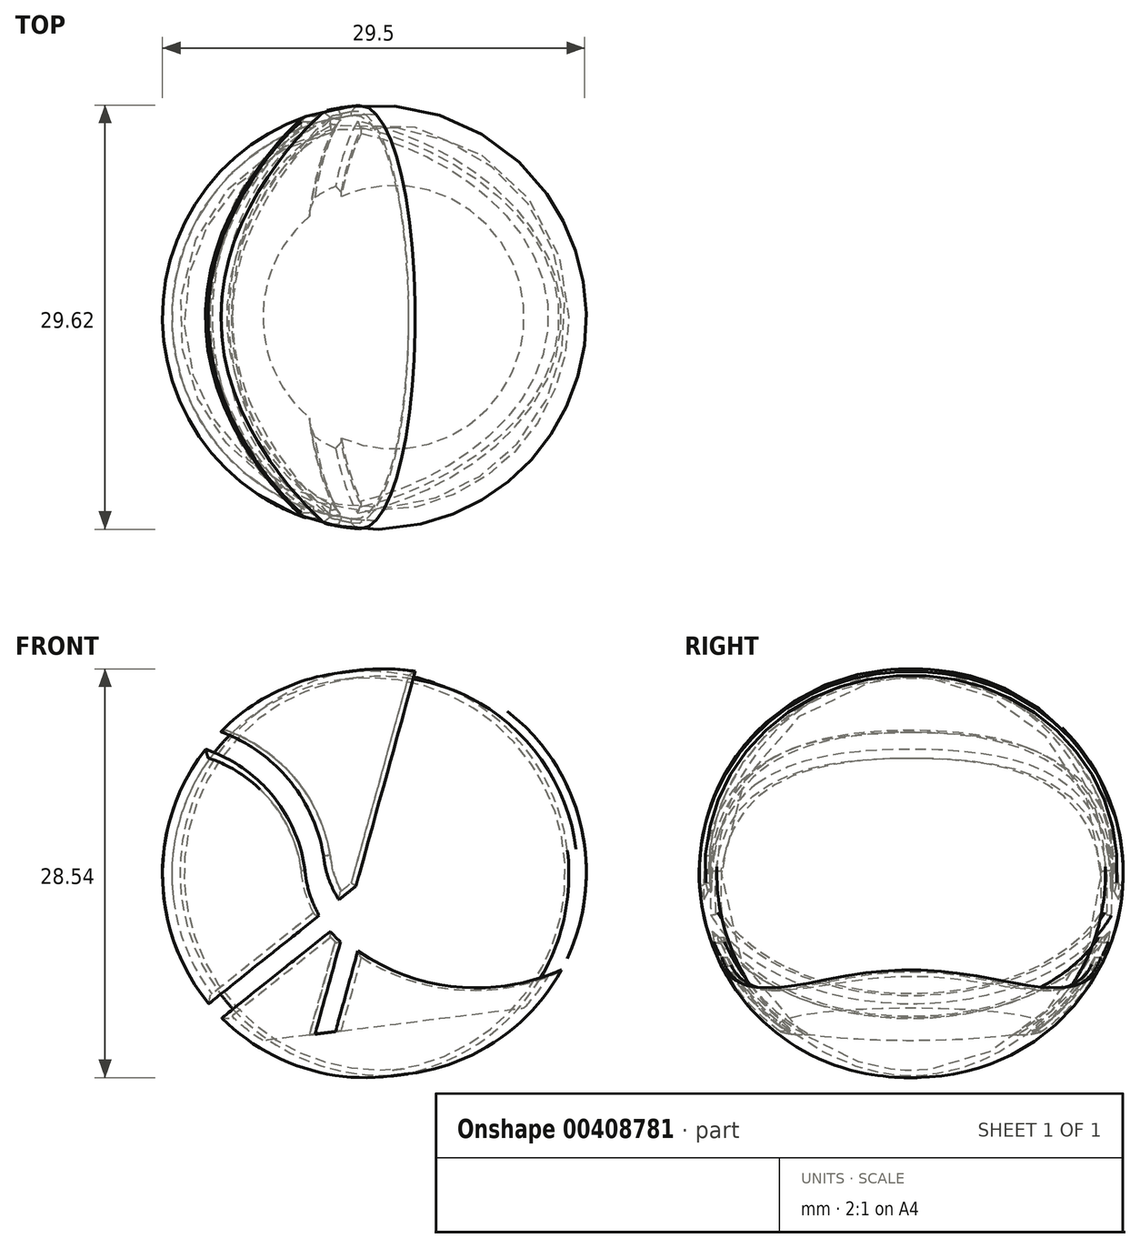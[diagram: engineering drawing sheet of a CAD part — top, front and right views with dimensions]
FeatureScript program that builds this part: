
annotation { "Feature Type Name" : "Feature", "Feature Type Description" : "" }
export const myFeature = defineFeature(function(context is Context, id is Id, definition is map)
    precondition{}
    {
        {
            var Q0;
            Q0=qCreatedBy(makeId("Front.planeOp"),FACE);
            var sketch = newSketch(context, id + "F0", { "sketchPlane" : qUnion([Q0])});
            skLineSegment(sketch, "E0", {"start": v(-42.37, 14.43) * mm, "end": v(-51.36, 13.33) * mm});
            skLineSegment(sketch, "E1", {"start": v(-51.36, 13.33) * mm, "end": v(-54.34, 37.59) * mm});
            skArc(sketch, "E2", {"start": v(-42.37, 14.43) * mm, "mid": v(-40.03, 30.31) * mm, "end": v(-54.34, 37.59) * mm});
            skSolve(sketch);
        }
        {
            var Q0;
            Q0=makeQuery(id+"F0.imprint","IMPRINT",FACE,{"disambiguationData":[TD([[makeQuery(id+"F0.imprint","IMPRINT",EDGE,{"derivedFrom":sQuery(id+"F0.wireOp",EDGE,"E0")}),-1.0]])]});
            var Q1;
            Q1=sQuery(id+"F0.wireOp",EDGE,"E1");
            revolve(context, id + "F1", {"entities" : qUnion([Q0]), "axis" : qUnion([Q1]), "revolveType" : RevolveType.FULL});
        }
        {
            var Q0;
            Q0=qCreatedBy(makeId("Front.planeOp"),FACE);
            var sketch = newSketch(context, id + "F2", { "sketchPlane" : qUnion([Q0])});
            skLineSegment(sketch, "E3", {"start": v(-47.67, 39.48) * mm, "end": v(-56.18, 8.75) * mm});
            skLineSegment(sketch, "E4", {"start": v(-56.18, 8.75) * mm, "end": v(-58.16, 9.3) * mm});
            skLineSegment(sketch, "E5", {"start": v(-58.16, 9.3) * mm, "end": v(-49.8, 39.48) * mm});
            skLineSegment(sketch, "E6", {"start": v(-49.8, 39.48) * mm, "end": v(-47.67, 39.48) * mm});
            skLineSegment(sketch, "E7", {"start": v(-65.5, 11.74) * mm, "end": v(-37.78, 33.85) * mm});
            skLineSegment(sketch, "E8", {"start": v(-37.78, 33.85) * mm, "end": v(-39.07, 35.47) * mm});
            skLineSegment(sketch, "E9", {"start": v(-39.07, 35.47) * mm, "end": v(-66.87, 13.3) * mm});
            skLineSegment(sketch, "E10", {"start": v(-66.87, 13.3) * mm, "end": v(-65.5, 11.74) * mm});
            skArc(sketch, "E11", {"start": v(-52.97, 20.32) * mm, "mid": v(-44.78, 17.68) * mm, "end": v(-37.04, 21.45) * mm});
            skPoint(sketch, "E11.startSnap0", {"position": v(-52.97, 24.38) * mm});
            skArc(sketch, "E12", {"start": v(-55.76, 25.21) * mm, "mid": v(-55.5, 23.95) * mm, "end": v(-55, 22.77) * mm});
            skArc(sketch, "E13", {"start": v(-55.76, 25.21) * mm, "mid": v(-58.82, 31.27) * mm, "end": v(-64.8, 34.46) * mm});
            skArc(sketch, "E14", {"start": v(-53.58, 18.12) * mm, "mid": v(-44.85, 15.85) * mm, "end": v(-36.46, 19.17) * mm});
            skArc(sketch, "E15", {"start": v(-57.79, 24.15) * mm, "mid": v(-57.05, 21.47) * mm, "end": v(-55.42, 19.21) * mm});
            skArc(sketch, "E16", {"start": v(-57.79, 24.15) * mm, "mid": v(-60.6, 29.8) * mm, "end": v(-66.32, 32.5) * mm});
            skLineSegment(sketch, "E17", {"start": v(-64.8, 34.46) * mm, "end": v(-66.32, 32.5) * mm});
            skLineSegment(sketch, "E18", {"start": v(-37.04, 21.45) * mm, "end": v(-36.46, 19.17) * mm});
            skSolve(sketch);
        }
        {
            var Q0;
            Q0 = qSketchRegion(id + "F2", true);
            extrude(context, id + "F3", {"entities" : qUnion([Q0]), "operationType" : NewBodyOperationType.ADD, "depth" : 18.8 * mm, "offsetDistance" : 25.4 * mm, "hasSecondDirection" : true, "secondDirectionOppositeDirection" : true, "secondDirectionDepth" : 18.8 * mm});
        }
        {
            var Q0;
            Q0=qCreatedBy(makeId("Front.planeOp"),FACE);
            var sketch = newSketch(context, id + "F4", { "sketchPlane" : qUnion([Q0])});
            skLineSegment(sketch, "E19", {"start": v(-54.57, 38.95) * mm, "end": v(-50.05, 3.12) * mm});
            skArc(sketch, "E20", {"start": v(-41.9, 14.18) * mm, "mid": v(-39.5, 30.68) * mm, "end": v(-54.46, 38.07) * mm});
            skLineSegment(sketch, "E21", {"start": v(-51.35, 13.45) * mm, "end": v(-41.4, 14.7) * mm});
            skLineSegment(sketch, "E22", {"start": v(-54.57, 38.95) * mm, "end": v(-55, 42.45) * mm});
            skLineSegment(sketch, "E23", {"start": v(-55, 42.45) * mm, "end": v(-20.73, 44.43) * mm});
            skLineSegment(sketch, "E24", {"start": v(-16.5, 6.68) * mm, "end": v(-50.05, 3.12) * mm});
            skLineSegment(sketch, "E25", {"start": v(-20.73, 44.43) * mm, "end": v(-16.5, 6.68) * mm});
            skSolve(sketch);
        }
        {
            var Q0;
            {var subQ0=sQuery(id+"F4.wireOp",EDGE,"E21");Q0=makeQuery(id+"F4.imprint","IMPRINT",FACE,{"disambiguationData":[TD([[makeQuery(id+"F4.imprint","IMPRINT",EDGE,{"derivedFrom":subQ0}),-1.0]])]});}
            var Q1;
            Q1=sQuery(id+"F4.wireOp",EDGE,"E19");
            revolve(context, id + "F5", {"operationType" : NewBodyOperationType.REMOVE, "entities" : qUnion([Q0]), "axis" : qUnion([Q1]), "revolveType" : RevolveType.FULL, "oppositeDirection" : true});
        }
        {
            var Q0;
            {var subQ0=sQuery(id+"F2.wireOp",EDGE,"E11");var subQ1=sQuery(id+"F2.wireOp",EDGE,"E8");var subQ2=sQuery(id+"F2.wireOp",EDGE,"E7");var subQ3=sQuery(id+"F2.wireOp",EDGE,"E3");Q0=makeQuery(id+"F5.boolean.opBoolean","INTERSECT",EDGE,{"derivedFrom":[makeQuery(id+"F3.boolean.opBoolean","SPLIT",FACE,{"disambiguationData":[TD([makeQuery(id+"F3.opExtrude","CAP_FACE",FACE,{"disambiguationData":[OSD([subQ3,sQuery(id+"F2.wireOp",EDGE,"E4"),sQuery(id+"F2.wireOp",EDGE,"E5"),sQuery(id+"F2.wireOp",EDGE,"E6"),subQ2,subQ1,sQuery(id+"F2.wireOp",EDGE,"E9"),sQuery(id+"F2.wireOp",EDGE,"E10"),subQ0,sQuery(id+"F2.wireOp",EDGE,"E12"),sQuery(id+"F2.wireOp",EDGE,"E13"),sQuery(id+"F2.wireOp",EDGE,"E14"),sQuery(id+"F2.wireOp",EDGE,"E15"),sQuery(id+"F2.wireOp",EDGE,"E16"),sQuery(id+"F2.wireOp",EDGE,"E17"),sQuery(id+"F2.wireOp",EDGE,"E18")])],"isStart":true})])],"derivedFrom":makeQuery(id+"F3.opExtrude","SWEPT_FACE",FACE,{"disambiguationData":[OSD([subQ3]),TDD([makeQuery(id+"F2.imprint","IMPRINT",EDGE,{"disambiguationData":[TD([[makeQuery(id+"F2.imprint","INTERSECT",VERTEX,{"derivedFrom":[subQ3,subQ0]}),1.0]])],"derivedFrom":subQ3})])]})}),makeQuery(id+"F5.opRevolve","SWEPT_FACE",FACE,{"disambiguationData":[OSD([sQuery(id+"F4.wireOp",EDGE,"E20")])]})]});}
            var Q1;
            Q1=makeQuery(id+"F5.boolean.opBoolean","INTERSECT",EDGE,{"derivedFrom":[makeQuery(id+"F3.opExtrude","SWEPT_FACE",FACE,{"disambiguationData":[OSD([sQuery(id+"F2.wireOp",EDGE,"E11")])]}),makeQuery(id+"F5.opRevolve","SWEPT_FACE",FACE,{"disambiguationData":[OSD([sQuery(id+"F4.wireOp",EDGE,"E20")])]})]});
            var Q2;
            {var subQ0=sQuery(id+"F2.wireOp",EDGE,"E7");Q2=makeQuery(id+"F5.boolean.opBoolean","INTERSECT",EDGE,{"derivedFrom":[makeQuery(id+"F3.opExtrude","SWEPT_FACE",FACE,{"disambiguationData":[OSD([subQ0]),TDD([makeQuery(id+"F2.imprint","IMPRINT",EDGE,{"disambiguationData":[TD([[makeQuery(id+"F2.imprint","INTERSECT",VERTEX,{"derivedFrom":[subQ0,sQuery(id+"F2.wireOp",EDGE,"E8")]}),1.0]])],"derivedFrom":subQ0})])]}),makeQuery(id+"F5.opRevolve","SWEPT_FACE",FACE,{"disambiguationData":[OSD([sQuery(id+"F4.wireOp",EDGE,"E20")])]})]});}
            var Q3;
            Q3=makeQuery(id+"F5.boolean.opBoolean","INTERSECT",EDGE,{"derivedFrom":[makeQuery(id+"F3.opExtrude","SWEPT_FACE",FACE,{"disambiguationData":[OSD([sQuery(id+"F2.wireOp",EDGE,"E14")])]}),makeQuery(id+"F5.opRevolve","SWEPT_FACE",FACE,{"disambiguationData":[OSD([sQuery(id+"F4.wireOp",EDGE,"E20")])]})]});
            var Q4;
            {var subQ0=sQuery(id+"F2.wireOp",EDGE,"E3");Q4=makeQuery(id+"F5.boolean.opBoolean","INTERSECT",EDGE,{"disambiguationData":[OD(0.0)],"derivedFrom":[makeQuery(id+"F3.opExtrude","SWEPT_FACE",FACE,{"disambiguationData":[OSD([subQ0]),TDD([makeQuery(id+"F2.imprint","IMPRINT",EDGE,{"disambiguationData":[TD([[makeQuery(id+"F2.imprint","INTERSECT",VERTEX,{"derivedFrom":[subQ0,sQuery(id+"F2.wireOp",EDGE,"E4")]}),1.0]])],"derivedFrom":subQ0})])]}),makeQuery(id+"F5.opRevolve","SWEPT_FACE",FACE,{"disambiguationData":[OSD([sQuery(id+"F4.wireOp",EDGE,"E20")])]})]});}
            var Q5;
            {var subQ0=sQuery(id+"F2.wireOp",EDGE,"E15");var subQ1=sQuery(id+"F2.wireOp",EDGE,"E10");var subQ2=sQuery(id+"F2.wireOp",EDGE,"E7");var subQ3=sQuery(id+"F2.wireOp",EDGE,"E5");var subQ4=sQuery(id+"F2.wireOp",EDGE,"E4");var subQ5=makeQuery(id+"F2.imprint","INTERSECT",VERTEX,{"derivedFrom":[subQ3,subQ0]});Q5=makeQuery(id+"F5.boolean.opBoolean","INTERSECT",EDGE,{"derivedFrom":[makeQuery(id+"F3.boolean.opBoolean","SPLIT",FACE,{"disambiguationData":[TD([makeQuery(id+"F3.opExtrude","CAP_FACE",FACE,{"disambiguationData":[OSD([sQuery(id+"F2.wireOp",EDGE,"E3"),subQ4,subQ3,sQuery(id+"F2.wireOp",EDGE,"E6"),subQ2,sQuery(id+"F2.wireOp",EDGE,"E8"),sQuery(id+"F2.wireOp",EDGE,"E9"),subQ1,sQuery(id+"F2.wireOp",EDGE,"E11"),sQuery(id+"F2.wireOp",EDGE,"E12"),sQuery(id+"F2.wireOp",EDGE,"E13"),sQuery(id+"F2.wireOp",EDGE,"E14"),subQ0,sQuery(id+"F2.wireOp",EDGE,"E16"),sQuery(id+"F2.wireOp",EDGE,"E17"),sQuery(id+"F2.wireOp",EDGE,"E18")])],"isStart":true})])],"derivedFrom":makeQuery(id+"F3.opExtrude","SWEPT_FACE",FACE,{"disambiguationData":[OSD([subQ0]),TDD([makeQuery(id+"F2.imprint","IMPRINT",EDGE,{"disambiguationData":[TD([[subQ5,1.0]])],"derivedFrom":subQ0})])]})}),makeQuery(id+"F5.opRevolve","SWEPT_FACE",FACE,{"disambiguationData":[OSD([sQuery(id+"F4.wireOp",EDGE,"E20")])]})]});}
            var Q6;
            {var subQ0=sQuery(id+"F2.wireOp",EDGE,"E5");Q6=makeQuery(id+"F5.boolean.opBoolean","INTERSECT",EDGE,{"disambiguationData":[OD(0.0)],"derivedFrom":[makeQuery(id+"F3.opExtrude","SWEPT_FACE",FACE,{"disambiguationData":[OSD([subQ0]),TDD([makeQuery(id+"F2.imprint","IMPRINT",EDGE,{"disambiguationData":[TD([[makeQuery(id+"F2.imprint","INTERSECT",VERTEX,{"derivedFrom":[sQuery(id+"F2.wireOp",EDGE,"E4"),subQ0]}),-1.0]])],"derivedFrom":subQ0})])]}),makeQuery(id+"F5.opRevolve","SWEPT_FACE",FACE,{"disambiguationData":[OSD([sQuery(id+"F4.wireOp",EDGE,"E20")])]})]});}
            var Q7;
            {var subQ0=sQuery(id+"F2.wireOp",EDGE,"E7");Q7=makeQuery(id+"F5.boolean.opBoolean","INTERSECT",EDGE,{"derivedFrom":[makeQuery(id+"F3.opExtrude","SWEPT_FACE",FACE,{"disambiguationData":[OSD([subQ0]),TDD([makeQuery(id+"F2.imprint","IMPRINT",EDGE,{"disambiguationData":[TD([[makeQuery(id+"F2.imprint","INTERSECT",VERTEX,{"derivedFrom":[subQ0,sQuery(id+"F2.wireOp",EDGE,"E10")]}),-1.0]])],"derivedFrom":subQ0})])]}),makeQuery(id+"F5.opRevolve","SWEPT_FACE",FACE,{"disambiguationData":[OSD([sQuery(id+"F4.wireOp",EDGE,"E20")])]})]});}
            var Q8;
            {var subQ0=sQuery(id+"F2.wireOp",EDGE,"E9");Q8=makeQuery(id+"F5.boolean.opBoolean","INTERSECT",EDGE,{"derivedFrom":[makeQuery(id+"F3.opExtrude","SWEPT_FACE",FACE,{"disambiguationData":[OSD([subQ0]),TDD([makeQuery(id+"F2.imprint","IMPRINT",EDGE,{"disambiguationData":[TD([[makeQuery(id+"F2.imprint","INTERSECT",VERTEX,{"derivedFrom":[sQuery(id+"F2.wireOp",EDGE,"E8"),subQ0]}),-1.0]])],"derivedFrom":subQ0})])]}),makeQuery(id+"F5.opRevolve","SWEPT_FACE",FACE,{"disambiguationData":[OSD([sQuery(id+"F4.wireOp",EDGE,"E20")])]})]});}
            var Q9;
            {var subQ0=sQuery(id+"F2.wireOp",EDGE,"E3");Q9=makeQuery(id+"F5.boolean.opBoolean","INTERSECT",EDGE,{"derivedFrom":[makeQuery(id+"F3.opExtrude","SWEPT_FACE",FACE,{"disambiguationData":[OSD([subQ0]),TDD([makeQuery(id+"F2.imprint","IMPRINT",EDGE,{"disambiguationData":[TD([[makeQuery(id+"F2.imprint","INTERSECT",VERTEX,{"derivedFrom":[subQ0,sQuery(id+"F2.wireOp",EDGE,"E6")]}),-1.0]])],"derivedFrom":subQ0})])]}),makeQuery(id+"F5.opRevolve","SWEPT_FACE",FACE,{"disambiguationData":[OSD([sQuery(id+"F4.wireOp",EDGE,"E20")])]})]});}
            var Q10;
            {var subQ0=sQuery(id+"F2.wireOp",EDGE,"E5");Q10=makeQuery(id+"F5.boolean.opBoolean","INTERSECT",EDGE,{"derivedFrom":[makeQuery(id+"F3.opExtrude","SWEPT_FACE",FACE,{"disambiguationData":[OSD([subQ0]),TDD([makeQuery(id+"F2.imprint","IMPRINT",EDGE,{"disambiguationData":[TD([[makeQuery(id+"F2.imprint","INTERSECT",VERTEX,{"derivedFrom":[subQ0,sQuery(id+"F2.wireOp",EDGE,"E6")]}),1.0]])],"derivedFrom":subQ0})])]}),makeQuery(id+"F5.opRevolve","SWEPT_FACE",FACE,{"disambiguationData":[OSD([sQuery(id+"F4.wireOp",EDGE,"E20")])]})]});}
            var Q11;
            {var subQ0=sQuery(id+"F2.wireOp",EDGE,"E12");var subQ1=sQuery(id+"F2.wireOp",EDGE,"E9");var subQ2=sQuery(id+"F2.wireOp",EDGE,"E6");var subQ3=sQuery(id+"F2.wireOp",EDGE,"E5");Q11=makeQuery(id+"F5.boolean.opBoolean","INTERSECT",EDGE,{"derivedFrom":[makeQuery(id+"F3.boolean.opBoolean","SPLIT",FACE,{"disambiguationData":[TD([makeQuery(id+"F3.opExtrude","CAP_FACE",FACE,{"disambiguationData":[OSD([sQuery(id+"F2.wireOp",EDGE,"E3"),sQuery(id+"F2.wireOp",EDGE,"E4"),subQ3,subQ2,sQuery(id+"F2.wireOp",EDGE,"E7"),sQuery(id+"F2.wireOp",EDGE,"E8"),subQ1,sQuery(id+"F2.wireOp",EDGE,"E10"),sQuery(id+"F2.wireOp",EDGE,"E11"),subQ0,sQuery(id+"F2.wireOp",EDGE,"E13"),sQuery(id+"F2.wireOp",EDGE,"E14"),sQuery(id+"F2.wireOp",EDGE,"E15"),sQuery(id+"F2.wireOp",EDGE,"E16"),sQuery(id+"F2.wireOp",EDGE,"E17"),sQuery(id+"F2.wireOp",EDGE,"E18")])],"isStart":true})])],"derivedFrom":makeQuery(id+"F3.opExtrude","SWEPT_FACE",FACE,{"disambiguationData":[OSD([subQ1]),TDD([makeQuery(id+"F2.imprint","IMPRINT",EDGE,{"disambiguationData":[TD([[makeQuery(id+"F2.imprint","INTERSECT",VERTEX,{"derivedFrom":[subQ1,subQ0]}),1.0]])],"derivedFrom":subQ1})])]})}),makeQuery(id+"F5.opRevolve","SWEPT_FACE",FACE,{"disambiguationData":[OSD([sQuery(id+"F4.wireOp",EDGE,"E20")])]})]});}
            var Q12;
            {var subQ0=sQuery(id+"F2.wireOp",EDGE,"E12");var subQ1=sQuery(id+"F2.wireOp",EDGE,"E9");var subQ2=sQuery(id+"F2.wireOp",EDGE,"E5");var subQ3=sQuery(id+"F2.wireOp",EDGE,"E13");Q12=makeQuery(id+"F5.boolean.opBoolean","INTERSECT",EDGE,{"derivedFrom":[makeQuery(id+"F3.boolean.opBoolean","SPLIT",FACE,{"disambiguationData":[TD([makeQuery(id+"F3.opExtrude","CAP_FACE",FACE,{"disambiguationData":[OSD([sQuery(id+"F2.wireOp",EDGE,"E3"),sQuery(id+"F2.wireOp",EDGE,"E4"),subQ2,sQuery(id+"F2.wireOp",EDGE,"E6"),sQuery(id+"F2.wireOp",EDGE,"E7"),sQuery(id+"F2.wireOp",EDGE,"E8"),subQ1,sQuery(id+"F2.wireOp",EDGE,"E10"),sQuery(id+"F2.wireOp",EDGE,"E11"),subQ0,subQ3,sQuery(id+"F2.wireOp",EDGE,"E14"),sQuery(id+"F2.wireOp",EDGE,"E15"),sQuery(id+"F2.wireOp",EDGE,"E16"),sQuery(id+"F2.wireOp",EDGE,"E17"),sQuery(id+"F2.wireOp",EDGE,"E18")])],"isStart":true})])],"derivedFrom":makeQuery(id+"F3.opExtrude","SWEPT_FACE",FACE,{"disambiguationData":[OSD([subQ0])]})}),makeQuery(id+"F5.opRevolve","SWEPT_FACE",FACE,{"disambiguationData":[OSD([sQuery(id+"F4.wireOp",EDGE,"E20")])]})]});}
            var Q13;
            Q13=makeQuery(id+"F5.boolean.opBoolean","INTERSECT",EDGE,{"derivedFrom":[makeQuery(id+"F3.opExtrude","SWEPT_FACE",FACE,{"disambiguationData":[OSD([sQuery(id+"F2.wireOp",EDGE,"E13")])]}),makeQuery(id+"F5.opRevolve","SWEPT_FACE",FACE,{"disambiguationData":[OSD([sQuery(id+"F4.wireOp",EDGE,"E20")])]})]});
            var Q14;
            Q14=makeQuery(id+"F5.boolean.opBoolean","INTERSECT",EDGE,{"derivedFrom":[makeQuery(id+"F3.opExtrude","SWEPT_FACE",FACE,{"disambiguationData":[OSD([sQuery(id+"F2.wireOp",EDGE,"E16")])]}),makeQuery(id+"F5.opRevolve","SWEPT_FACE",FACE,{"disambiguationData":[OSD([sQuery(id+"F4.wireOp",EDGE,"E20")])]})]});
            var Q15;
            {var subQ0=sQuery(id+"F2.wireOp",EDGE,"E16");var subQ1=sQuery(id+"F2.wireOp",EDGE,"E15");var subQ2=sQuery(id+"F2.wireOp",EDGE,"E10");var subQ3=sQuery(id+"F2.wireOp",EDGE,"E9");Q15=makeQuery(id+"F5.boolean.opBoolean","INTERSECT",EDGE,{"derivedFrom":[makeQuery(id+"F3.boolean.opBoolean","SPLIT",FACE,{"disambiguationData":[TD([makeQuery(id+"F3.opExtrude","CAP_FACE",FACE,{"disambiguationData":[OSD([sQuery(id+"F2.wireOp",EDGE,"E3"),sQuery(id+"F2.wireOp",EDGE,"E4"),sQuery(id+"F2.wireOp",EDGE,"E5"),sQuery(id+"F2.wireOp",EDGE,"E6"),sQuery(id+"F2.wireOp",EDGE,"E7"),sQuery(id+"F2.wireOp",EDGE,"E8"),subQ3,subQ2,sQuery(id+"F2.wireOp",EDGE,"E11"),sQuery(id+"F2.wireOp",EDGE,"E12"),sQuery(id+"F2.wireOp",EDGE,"E13"),sQuery(id+"F2.wireOp",EDGE,"E14"),subQ1,subQ0,sQuery(id+"F2.wireOp",EDGE,"E17"),sQuery(id+"F2.wireOp",EDGE,"E18")])],"isStart":true})])],"derivedFrom":makeQuery(id+"F3.opExtrude","SWEPT_FACE",FACE,{"disambiguationData":[OSD([subQ1]),TDD([makeQuery(id+"F2.imprint","IMPRINT",EDGE,{"disambiguationData":[TD([[makeQuery(id+"F2.imprint","INTERSECT",VERTEX,{"derivedFrom":[subQ1,subQ0]}),-1.0]])],"derivedFrom":subQ1})])]})}),makeQuery(id+"F5.opRevolve","SWEPT_FACE",FACE,{"disambiguationData":[OSD([sQuery(id+"F4.wireOp",EDGE,"E20")])]})]});}
            var Q16;
            {var subQ0=sQuery(id+"F2.wireOp",EDGE,"E9");Q16=makeQuery(id+"F5.boolean.opBoolean","INTERSECT",EDGE,{"derivedFrom":[makeQuery(id+"F3.opExtrude","SWEPT_FACE",FACE,{"disambiguationData":[OSD([subQ0]),TDD([makeQuery(id+"F2.imprint","IMPRINT",EDGE,{"disambiguationData":[TD([[makeQuery(id+"F2.imprint","INTERSECT",VERTEX,{"derivedFrom":[subQ0,sQuery(id+"F2.wireOp",EDGE,"E10")]}),1.0]])],"derivedFrom":subQ0})])]}),makeQuery(id+"F5.opRevolve","SWEPT_FACE",FACE,{"disambiguationData":[OSD([sQuery(id+"F4.wireOp",EDGE,"E20")])]})]});}
            var Q17;
            {var subQ0=sQuery(id+"F2.wireOp",EDGE,"E16");var subQ1=sQuery(id+"F2.wireOp",EDGE,"E15");var subQ2=sQuery(id+"F2.wireOp",EDGE,"E10");var subQ3=sQuery(id+"F2.wireOp",EDGE,"E9");Q17=makeQuery(id+"F5.boolean.opBoolean","INTERSECT",EDGE,{"derivedFrom":[makeQuery(id+"F3.boolean.opBoolean","SPLIT",FACE,{"disambiguationData":[TD([makeQuery(id+"F3.opExtrude","CAP_FACE",FACE,{"disambiguationData":[OSD([sQuery(id+"F2.wireOp",EDGE,"E3"),sQuery(id+"F2.wireOp",EDGE,"E4"),sQuery(id+"F2.wireOp",EDGE,"E5"),sQuery(id+"F2.wireOp",EDGE,"E6"),sQuery(id+"F2.wireOp",EDGE,"E7"),sQuery(id+"F2.wireOp",EDGE,"E8"),subQ3,subQ2,sQuery(id+"F2.wireOp",EDGE,"E11"),sQuery(id+"F2.wireOp",EDGE,"E12"),sQuery(id+"F2.wireOp",EDGE,"E13"),sQuery(id+"F2.wireOp",EDGE,"E14"),subQ1,subQ0,sQuery(id+"F2.wireOp",EDGE,"E17"),sQuery(id+"F2.wireOp",EDGE,"E18")])],"isStart":false})])],"derivedFrom":makeQuery(id+"F3.opExtrude","SWEPT_FACE",FACE,{"disambiguationData":[OSD([subQ1]),TDD([makeQuery(id+"F2.imprint","IMPRINT",EDGE,{"disambiguationData":[TD([[makeQuery(id+"F2.imprint","INTERSECT",VERTEX,{"derivedFrom":[subQ1,subQ0]}),-1.0]])],"derivedFrom":subQ1})])]})}),makeQuery(id+"F5.opRevolve","SWEPT_FACE",FACE,{"disambiguationData":[OSD([sQuery(id+"F4.wireOp",EDGE,"E20")])]})]});}
            var Q18;
            {var subQ0=sQuery(id+"F2.wireOp",EDGE,"E12");var subQ1=sQuery(id+"F2.wireOp",EDGE,"E9");var subQ2=sQuery(id+"F2.wireOp",EDGE,"E5");var subQ3=sQuery(id+"F2.wireOp",EDGE,"E13");Q18=makeQuery(id+"F5.boolean.opBoolean","INTERSECT",EDGE,{"derivedFrom":[makeQuery(id+"F3.boolean.opBoolean","SPLIT",FACE,{"disambiguationData":[TD([makeQuery(id+"F3.opExtrude","CAP_FACE",FACE,{"disambiguationData":[OSD([sQuery(id+"F2.wireOp",EDGE,"E3"),sQuery(id+"F2.wireOp",EDGE,"E4"),subQ2,sQuery(id+"F2.wireOp",EDGE,"E6"),sQuery(id+"F2.wireOp",EDGE,"E7"),sQuery(id+"F2.wireOp",EDGE,"E8"),subQ1,sQuery(id+"F2.wireOp",EDGE,"E10"),sQuery(id+"F2.wireOp",EDGE,"E11"),subQ0,subQ3,sQuery(id+"F2.wireOp",EDGE,"E14"),sQuery(id+"F2.wireOp",EDGE,"E15"),sQuery(id+"F2.wireOp",EDGE,"E16"),sQuery(id+"F2.wireOp",EDGE,"E17"),sQuery(id+"F2.wireOp",EDGE,"E18")])],"isStart":false})])],"derivedFrom":makeQuery(id+"F3.opExtrude","SWEPT_FACE",FACE,{"disambiguationData":[OSD([subQ0])]})}),makeQuery(id+"F5.opRevolve","SWEPT_FACE",FACE,{"disambiguationData":[OSD([sQuery(id+"F4.wireOp",EDGE,"E20")])]})]});}
            var Q19;
            {var subQ0=sQuery(id+"F2.wireOp",EDGE,"E12");var subQ1=sQuery(id+"F2.wireOp",EDGE,"E9");var subQ2=sQuery(id+"F2.wireOp",EDGE,"E6");var subQ3=sQuery(id+"F2.wireOp",EDGE,"E5");Q19=makeQuery(id+"F5.boolean.opBoolean","INTERSECT",EDGE,{"derivedFrom":[makeQuery(id+"F3.boolean.opBoolean","SPLIT",FACE,{"disambiguationData":[TD([makeQuery(id+"F3.opExtrude","CAP_FACE",FACE,{"disambiguationData":[OSD([sQuery(id+"F2.wireOp",EDGE,"E3"),sQuery(id+"F2.wireOp",EDGE,"E4"),subQ3,subQ2,sQuery(id+"F2.wireOp",EDGE,"E7"),sQuery(id+"F2.wireOp",EDGE,"E8"),subQ1,sQuery(id+"F2.wireOp",EDGE,"E10"),sQuery(id+"F2.wireOp",EDGE,"E11"),subQ0,sQuery(id+"F2.wireOp",EDGE,"E13"),sQuery(id+"F2.wireOp",EDGE,"E14"),sQuery(id+"F2.wireOp",EDGE,"E15"),sQuery(id+"F2.wireOp",EDGE,"E16"),sQuery(id+"F2.wireOp",EDGE,"E17"),sQuery(id+"F2.wireOp",EDGE,"E18")])],"isStart":false})])],"derivedFrom":makeQuery(id+"F3.opExtrude","SWEPT_FACE",FACE,{"disambiguationData":[OSD([subQ1]),TDD([makeQuery(id+"F2.imprint","IMPRINT",EDGE,{"disambiguationData":[TD([[makeQuery(id+"F2.imprint","INTERSECT",VERTEX,{"derivedFrom":[subQ1,subQ0]}),1.0]])],"derivedFrom":subQ1})])]})}),makeQuery(id+"F5.opRevolve","SWEPT_FACE",FACE,{"disambiguationData":[OSD([sQuery(id+"F4.wireOp",EDGE,"E20")])]})]});}
            var Q20;
            {var subQ0=sQuery(id+"F2.wireOp",EDGE,"E11");var subQ1=sQuery(id+"F2.wireOp",EDGE,"E8");var subQ2=sQuery(id+"F2.wireOp",EDGE,"E7");var subQ3=sQuery(id+"F2.wireOp",EDGE,"E3");Q20=makeQuery(id+"F5.boolean.opBoolean","INTERSECT",EDGE,{"derivedFrom":[makeQuery(id+"F3.boolean.opBoolean","SPLIT",FACE,{"disambiguationData":[TD([makeQuery(id+"F3.opExtrude","CAP_FACE",FACE,{"disambiguationData":[OSD([subQ3,sQuery(id+"F2.wireOp",EDGE,"E4"),sQuery(id+"F2.wireOp",EDGE,"E5"),sQuery(id+"F2.wireOp",EDGE,"E6"),subQ2,subQ1,sQuery(id+"F2.wireOp",EDGE,"E9"),sQuery(id+"F2.wireOp",EDGE,"E10"),subQ0,sQuery(id+"F2.wireOp",EDGE,"E12"),sQuery(id+"F2.wireOp",EDGE,"E13"),sQuery(id+"F2.wireOp",EDGE,"E14"),sQuery(id+"F2.wireOp",EDGE,"E15"),sQuery(id+"F2.wireOp",EDGE,"E16"),sQuery(id+"F2.wireOp",EDGE,"E17"),sQuery(id+"F2.wireOp",EDGE,"E18")])],"isStart":false})])],"derivedFrom":makeQuery(id+"F3.opExtrude","SWEPT_FACE",FACE,{"disambiguationData":[OSD([subQ3]),TDD([makeQuery(id+"F2.imprint","IMPRINT",EDGE,{"disambiguationData":[TD([[makeQuery(id+"F2.imprint","INTERSECT",VERTEX,{"derivedFrom":[subQ3,subQ0]}),1.0]])],"derivedFrom":subQ3})])]})}),makeQuery(id+"F5.opRevolve","SWEPT_FACE",FACE,{"disambiguationData":[OSD([sQuery(id+"F4.wireOp",EDGE,"E20")])]})]});}
            var Q21;
            {var subQ0=sQuery(id+"F2.wireOp",EDGE,"E5");Q21=makeQuery(id+"F5.boolean.opBoolean","INTERSECT",EDGE,{"disambiguationData":[OD(1.0)],"derivedFrom":[makeQuery(id+"F3.opExtrude","SWEPT_FACE",FACE,{"disambiguationData":[OSD([subQ0]),TDD([makeQuery(id+"F2.imprint","IMPRINT",EDGE,{"disambiguationData":[TD([[makeQuery(id+"F2.imprint","INTERSECT",VERTEX,{"derivedFrom":[sQuery(id+"F2.wireOp",EDGE,"E4"),subQ0]}),-1.0]])],"derivedFrom":subQ0})])]}),makeQuery(id+"F5.opRevolve","SWEPT_FACE",FACE,{"disambiguationData":[OSD([sQuery(id+"F4.wireOp",EDGE,"E20")])]})]});}
            var Q22;
            {var subQ0=sQuery(id+"F2.wireOp",EDGE,"E15");var subQ1=sQuery(id+"F2.wireOp",EDGE,"E10");var subQ2=sQuery(id+"F2.wireOp",EDGE,"E7");var subQ3=sQuery(id+"F2.wireOp",EDGE,"E5");var subQ4=sQuery(id+"F2.wireOp",EDGE,"E4");var subQ5=makeQuery(id+"F2.imprint","INTERSECT",VERTEX,{"derivedFrom":[subQ3,subQ0]});Q22=makeQuery(id+"F5.boolean.opBoolean","INTERSECT",EDGE,{"derivedFrom":[makeQuery(id+"F3.boolean.opBoolean","SPLIT",FACE,{"disambiguationData":[TD([makeQuery(id+"F3.opExtrude","CAP_FACE",FACE,{"disambiguationData":[OSD([sQuery(id+"F2.wireOp",EDGE,"E3"),subQ4,subQ3,sQuery(id+"F2.wireOp",EDGE,"E6"),subQ2,sQuery(id+"F2.wireOp",EDGE,"E8"),sQuery(id+"F2.wireOp",EDGE,"E9"),subQ1,sQuery(id+"F2.wireOp",EDGE,"E11"),sQuery(id+"F2.wireOp",EDGE,"E12"),sQuery(id+"F2.wireOp",EDGE,"E13"),sQuery(id+"F2.wireOp",EDGE,"E14"),subQ0,sQuery(id+"F2.wireOp",EDGE,"E16"),sQuery(id+"F2.wireOp",EDGE,"E17"),sQuery(id+"F2.wireOp",EDGE,"E18")])],"isStart":false})])],"derivedFrom":makeQuery(id+"F3.opExtrude","SWEPT_FACE",FACE,{"disambiguationData":[OSD([subQ0]),TDD([makeQuery(id+"F2.imprint","IMPRINT",EDGE,{"disambiguationData":[TD([[subQ5,1.0]])],"derivedFrom":subQ0})])]})}),makeQuery(id+"F5.opRevolve","SWEPT_FACE",FACE,{"disambiguationData":[OSD([sQuery(id+"F4.wireOp",EDGE,"E20")])]})]});}
            var Q23;
            {var subQ0=sQuery(id+"F2.wireOp",EDGE,"E3");Q23=makeQuery(id+"F5.boolean.opBoolean","INTERSECT",EDGE,{"disambiguationData":[OD(1.0)],"derivedFrom":[makeQuery(id+"F3.opExtrude","SWEPT_FACE",FACE,{"disambiguationData":[OSD([subQ0]),TDD([makeQuery(id+"F2.imprint","IMPRINT",EDGE,{"disambiguationData":[TD([[makeQuery(id+"F2.imprint","INTERSECT",VERTEX,{"derivedFrom":[subQ0,sQuery(id+"F2.wireOp",EDGE,"E4")]}),1.0]])],"derivedFrom":subQ0})])]}),makeQuery(id+"F5.opRevolve","SWEPT_FACE",FACE,{"disambiguationData":[OSD([sQuery(id+"F4.wireOp",EDGE,"E20")])]})]});}
            chamfer(context, id + "F6", {"entities" : qUnion([Q0, Q1, Q2, Q3, Q4, Q5, Q6, Q7, Q8, Q9, Q10, Q11, Q12, Q13, Q14, Q15, Q16, Q17, Q18, Q19, Q20, Q21, Q22, Q23]), "width" : 0.38 * mm, "tangentPropagation" : true});
        }
    });
